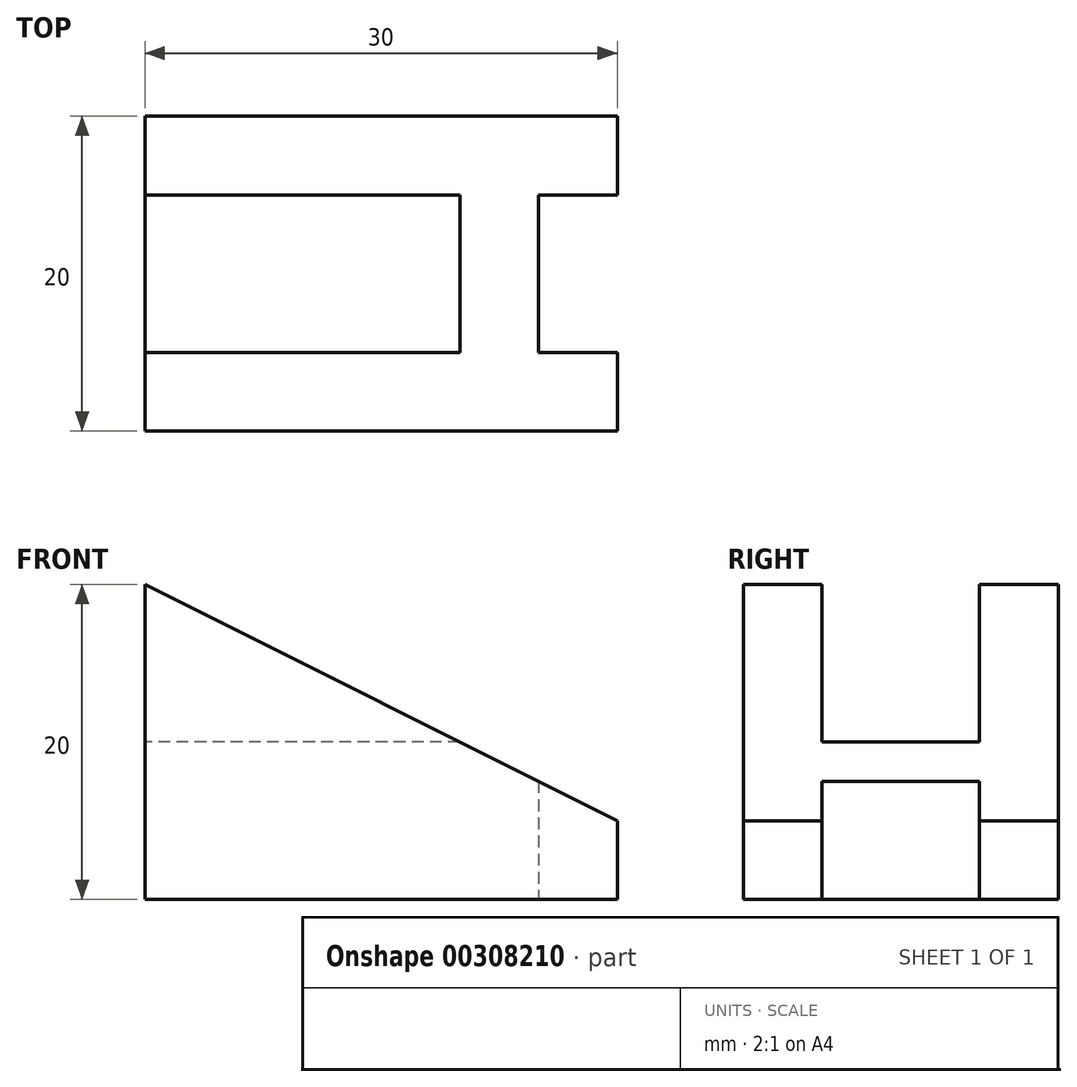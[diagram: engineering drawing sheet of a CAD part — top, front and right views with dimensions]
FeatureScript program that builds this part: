
annotation { "Feature Type Name" : "Feature", "Feature Type Description" : "" }
export const myFeature = defineFeature(function(context is Context, id is Id, definition is map)
    precondition{}
    {
        {
            var Q0;
            Q0=qCreatedBy(makeId("Front.planeOp"),FACE);
            var sketch = newSketch(context, id + "F0", { "sketchPlane" : qUnion([Q0])});
            skLineSegment(sketch, "E0", {"start": v(0, 0) * mm, "end": v(30, 0) * mm});
            skLineSegment(sketch, "E1", {"start": v(30, 0) * mm, "end": v(30, 20) * mm});
            skLineSegment(sketch, "E2", {"start": v(30, 20) * mm, "end": v(0, 20) * mm});
            skLineSegment(sketch, "E3", {"start": v(0, 20) * mm, "end": v(0, 0) * mm});
            skSolve(sketch);
        }
        {
            var Q0;
            Q0 = qSketchRegion(id + "F0", true);
            extrude(context, id + "F1", {"entities" : qUnion([Q0]), "endBound" : BoundingType.SYMMETRIC, "depth" : 20 * mm});
        }
        {
            var Q0;
            Q0=makeQuery(id+"F1.opExtrude","CAP_FACE",FACE,{"disambiguationData":[OSD([sQuery(id+"F0.wireOp",EDGE,"E0"),sQuery(id+"F0.wireOp",EDGE,"E1"),sQuery(id+"F0.wireOp",EDGE,"E2"),sQuery(id+"F0.wireOp",EDGE,"E3")])],"isStart":false});
            var sketch = newSketch(context, id + "F2", { "sketchPlane" : qUnion([Q0])});
            skLineSegment(sketch, "E4", {"start": v(0, 20) * mm, "end": v(30, 5) * mm});
            skSolve(sketch);
        }
        {
            var Q0;
            {var subQ0=sQuery(id+"F2.wireOp",EDGE,"E4");Q0=makeQuery(id+"F2.imprint","IMPRINT",FACE,{"disambiguationData":[TD([[makeQuery(id+"F2.imprint","IMPRINT",EDGE,{"derivedFrom":subQ0}),1.0]])]});}
            extrude(context, id + "F3", {"entities" : qUnion([Q0]), "operationType" : NewBodyOperationType.REMOVE, "endBound" : BoundingType.THROUGH_ALL, "oppositeDirection" : true, "depth" : 25 * mm});
        }
        {
            var Q0;
            Q0=makeQuery(id+"F1.opExtrude","SWEPT_FACE",FACE,{"disambiguationData":[OSD([sQuery(id+"F0.wireOp",EDGE,"E3")])]});
            var sketch = newSketch(context, id + "F4", { "sketchPlane" : qUnion([Q0])});
            skLineSegment(sketch, "E5", {"start": v(-5, 20) * mm, "end": v(-5, 10) * mm});
            skLineSegment(sketch, "E6", {"start": v(-5, 10) * mm, "end": v(5, 10) * mm});
            skLineSegment(sketch, "E7", {"start": v(5, 10) * mm, "end": v(5, 20) * mm});
            skLineSegment(sketch, "E8", {"start": v(-5, 10) * mm, "end": v(0, 0) * mm, "construction": true});
            skLineSegment(sketch, "E9", {"start": v(0, 0) * mm, "end": v(5, 10) * mm, "construction": true});
            skSolve(sketch);
        }
        {
            var Q0;
            {var subQ0=sQuery(id+"F4.wireOp",EDGE,"E5");Q0=makeQuery(id+"F4.imprint","IMPRINT",FACE,{"disambiguationData":[TD([[makeQuery(id+"F4.imprint","IMPRINT",EDGE,{"derivedFrom":subQ0}),1.0]])]});}
            extrude(context, id + "F5", {"entities" : qUnion([Q0]), "operationType" : NewBodyOperationType.REMOVE, "endBound" : BoundingType.THROUGH_ALL, "oppositeDirection" : true, "depth" : 25 * mm});
        }
        {
            var Q0;
            Q0=makeQuery(id+"F1.opExtrude","SWEPT_FACE",FACE,{"disambiguationData":[OSD([sQuery(id+"F0.wireOp",EDGE,"E0")])]});
            var sketch = newSketch(context, id + "F6", { "sketchPlane" : qUnion([Q0])});
            skLineSegment(sketch, "E10", {"start": v(30, 5) * mm, "end": v(25, 5) * mm});
            skLineSegment(sketch, "E11", {"start": v(25, 5) * mm, "end": v(25, -5) * mm});
            skLineSegment(sketch, "E12", {"start": v(25, -5) * mm, "end": v(30, -5) * mm});
            skLineSegment(sketch, "E13", {"start": v(0, 0) * mm, "end": v(25, 5) * mm, "construction": true});
            skLineSegment(sketch, "E14", {"start": v(0, 0) * mm, "end": v(25, -5) * mm, "construction": true});
            skSolve(sketch);
        }
        {
            var Q0;
            {var subQ0=sQuery(id+"F6.wireOp",EDGE,"E10");Q0=makeQuery(id+"F6.imprint","IMPRINT",FACE,{"disambiguationData":[TD([[makeQuery(id+"F6.imprint","IMPRINT",EDGE,{"derivedFrom":subQ0}),1.0]])]});}
            extrude(context, id + "F7", {"entities" : qUnion([Q0]), "operationType" : NewBodyOperationType.REMOVE, "endBound" : BoundingType.THROUGH_ALL, "oppositeDirection" : true, "depth" : 25 * mm});
        }
    });
